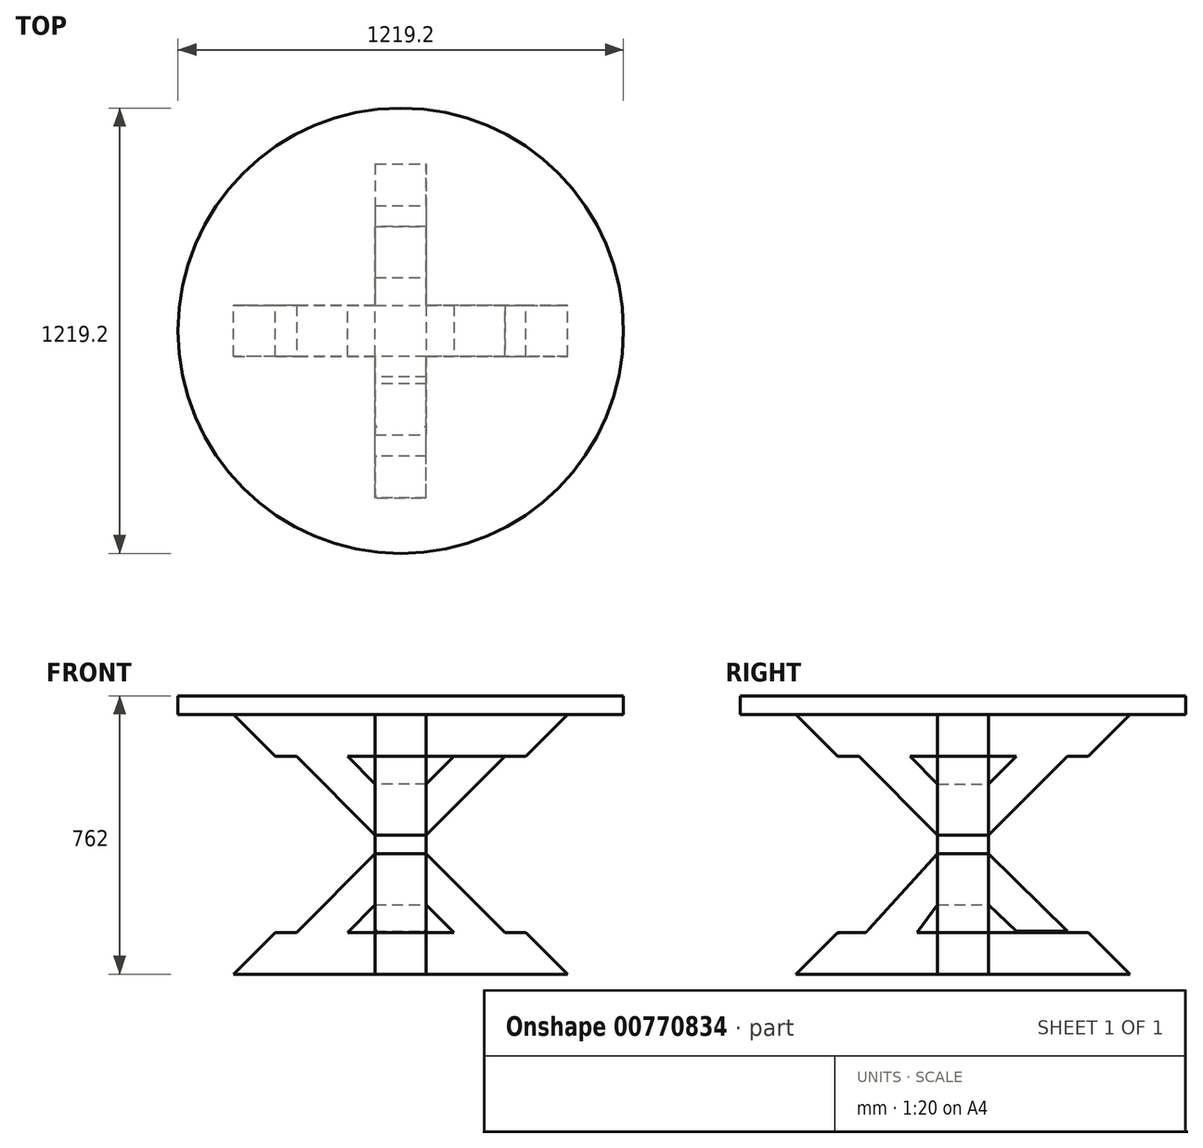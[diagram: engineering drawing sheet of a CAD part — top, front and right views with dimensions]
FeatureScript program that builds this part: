
annotation { "Feature Type Name" : "Feature", "Feature Type Description" : "" }
export const myFeature = defineFeature(function(context is Context, id is Id, definition is map)
    precondition{}
    {
        {
            var Q0;
            Q0=qCreatedBy(makeId("Top.planeOp"),FACE);
            var sketch = newSketch(context, id + "F0", { "sketchPlane" : qUnion([Q0])});
            skLineSegment(sketch, "E0.bottom", {"start": v(-457.2, -69.85) * mm, "end": v(457.2, -69.85) * mm});
            skLineSegment(sketch, "E0.top", {"start": v(-457.2, 69.85) * mm, "end": v(457.2, 69.85) * mm});
            skLineSegment(sketch, "E0.left", {"start": v(-457.2, -69.85) * mm, "end": v(-457.2, 69.85) * mm});
            skLineSegment(sketch, "E0.right", {"start": v(457.2, -69.85) * mm, "end": v(457.2, 69.85) * mm});
            skPoint(sketch, "E0.middle", {"position": v(0, 0) * mm});
            skSolve(sketch);
        }
        {
            var Q0;
            Q0 = qSketchRegion(id + "F0", true);
            extrude(context, id + "F1", {"entities" : qUnion([Q0]), "depth" : 38.1 * mm, "offsetDistance" : 25.4 * mm});
        }
        {
            var Q0;
            Q0=makeQuery(id+"F1.opExtrude","CAP_EDGE",EDGE,{"disambiguationData":[OSD([sQuery(id+"F0.wireOp",EDGE,"E0.left")])],"isStart":false});
            chamfer(context, id + "F2", {"entities" : qUnion([Q0]), "width" : 38.1 * mm, "tangentPropagation" : true});
        }
        {
            var Q0;
            Q0=makeQuery(id+"F1.opExtrude","CAP_EDGE",EDGE,{"disambiguationData":[OSD([sQuery(id+"F0.wireOp",EDGE,"E0.right")])],"isStart":false});
            chamfer(context, id + "F3", {"entities" : qUnion([Q0]), "width" : 38.1 * mm, "tangentPropagation" : true});
        }
        {
            var Q0;
            Q0=makeQuery(id+"F1.opExtrude","CAP_FACE",FACE,{"disambiguationData":[OSD([sQuery(id+"F0.wireOp",EDGE,"E0.bottom"),sQuery(id+"F0.wireOp",EDGE,"E0.top"),sQuery(id+"F0.wireOp",EDGE,"E0.left"),sQuery(id+"F0.wireOp",EDGE,"E0.right")])],"isStart":false});
            var sketch = newSketch(context, id + "F4", { "sketchPlane" : qUnion([Q0])});
            skLineSegment(sketch, "E1.bottom", {"start": v(419.1, 69.85) * mm, "end": v(-419.1, 69.85) * mm});
            skLineSegment(sketch, "E1.top", {"start": v(419.1, -69.85) * mm, "end": v(-419.1, -69.85) * mm});
            skLineSegment(sketch, "E1.left", {"start": v(419.1, 69.85) * mm, "end": v(419.1, -69.85) * mm});
            skLineSegment(sketch, "E1.right", {"start": v(-419.1, 69.85) * mm, "end": v(-419.1, -69.85) * mm});
            skPoint(sketch, "E1.middle", {"position": v(0, 0) * mm});
            skSolve(sketch);
        }
        {
            var Q0;
            Q0 = qSketchRegion(id + "F4", true);
            extrude(context, id + "F5", {"entities" : qUnion([Q0]), "operationType" : NewBodyOperationType.ADD, "depth" : 38.1 * mm, "offsetDistance" : 25.4 * mm});
        }
        {
            var Q0;
            Q0=makeQuery(id+"F5.opExtrude","CAP_EDGE",EDGE,{"disambiguationData":[OSD([sQuery(id+"F4.wireOp",EDGE,"E1.right")])],"isStart":false});
            chamfer(context, id + "F6", {"entities" : qUnion([Q0]), "width" : 38.1 * mm, "tangentPropagation" : true});
        }
        {
            var Q0;
            Q0=makeQuery(id+"F5.opExtrude","CAP_EDGE",EDGE,{"disambiguationData":[OSD([sQuery(id+"F4.wireOp",EDGE,"E1.left")])],"isStart":false});
            chamfer(context, id + "F7", {"entities" : qUnion([Q0]), "width" : 38.1 * mm, "tangentPropagation" : true});
        }
        {
            var Q0;
            Q0=makeQuery(id+"F5.opExtrude","CAP_FACE",FACE,{"disambiguationData":[OSD([sQuery(id+"F4.wireOp",EDGE,"E1.bottom"),sQuery(id+"F4.wireOp",EDGE,"E1.top"),sQuery(id+"F4.wireOp",EDGE,"E1.left"),sQuery(id+"F4.wireOp",EDGE,"E1.right")])],"isStart":false});
            var sketch = newSketch(context, id + "F8", { "sketchPlane" : qUnion([Q0])});
            skLineSegment(sketch, "E2.bottom", {"start": v(-381, 69.85) * mm, "end": v(381, 69.85) * mm});
            skLineSegment(sketch, "E2.top", {"start": v(-381, -69.85) * mm, "end": v(381, -69.85) * mm});
            skLineSegment(sketch, "E2.left", {"start": v(-381, 69.85) * mm, "end": v(-381, -69.85) * mm});
            skLineSegment(sketch, "E2.right", {"start": v(381, 69.85) * mm, "end": v(381, -69.85) * mm});
            skPoint(sketch, "E2.middle", {"position": v(0, 0) * mm});
            skSolve(sketch);
        }
        {
            var Q0;
            Q0 = qSketchRegion(id + "F8", true);
            extrude(context, id + "F9", {"entities" : qUnion([Q0]), "operationType" : NewBodyOperationType.ADD, "depth" : 38.1 * mm, "offsetDistance" : 25.4 * mm});
        }
        {
            var Q0;
            Q0=makeQuery(id+"F9.opExtrude","CAP_EDGE",EDGE,{"disambiguationData":[OSD([sQuery(id+"F8.wireOp",EDGE,"E2.left")])],"isStart":false});
            var Q1;
            Q1=makeQuery(id+"F9.opExtrude","CAP_EDGE",EDGE,{"disambiguationData":[OSD([sQuery(id+"F8.wireOp",EDGE,"E2.right")])],"isStart":false});
            chamfer(context, id + "F10", {"entities" : qUnion([Q0, Q1]), "width" : 38.1 * mm, "tangentPropagation" : true});
        }
        {
            var Q0;
            Q0=makeQuery(id+"F9.boolean.opBoolean","MERGE",FACE,{"derivedFrom":[makeQuery(id+"F5.boolean.opBoolean","MERGE",FACE,{"derivedFrom":[makeQuery(id+"F1.opExtrude","SWEPT_FACE",FACE,{"disambiguationData":[OSD([sQuery(id+"F0.wireOp",EDGE,"E0.bottom")])]}),makeQuery(id+"F5.opExtrude","SWEPT_FACE",FACE,{"disambiguationData":[OSD([sQuery(id+"F4.wireOp",EDGE,"E1.top")])]})]}),makeQuery(id+"F9.opExtrude","SWEPT_FACE",FACE,{"disambiguationData":[OSD([sQuery(id+"F8.wireOp",EDGE,"E2.top")])]})]});
            var sketch = newSketch(context, id + "F11", { "sketchPlane" : qUnion([Q0])});
            skLineSegment(sketch, "E3.bottom", {"start": v(-69.85, 0) * mm, "end": v(69.85, 0) * mm});
            skLineSegment(sketch, "E3.top", {"start": v(-69.85, 114.3) * mm, "end": v(69.85, 114.3) * mm});
            skLineSegment(sketch, "E3.left", {"start": v(-69.85, 0) * mm, "end": v(-69.85, 114.3) * mm});
            skLineSegment(sketch, "E3.right", {"start": v(69.85, 0) * mm, "end": v(69.85, 114.3) * mm});
            skSolve(sketch);
        }
        {
            var Q0;
            Q0 = qSketchRegion(id + "F11", true);
            var Q1;
            Q1=makeQuery(id+"F11.imprint","IMPRINT",FACE,{"disambiguationData":[TD([[makeQuery(id+"F11.imprint","IMPRINT",EDGE,{"derivedFrom":sQuery(id+"F11.wireOp",EDGE,"E3.bottom")}),1.0]])]});
            extrude(context, id + "F12", {"entities" : qUnion([Q0, Q1]), "operationType" : NewBodyOperationType.ADD, "depth" : 387.35 * mm, "offsetDistance" : 25.4 * mm});
        }
        {
            var Q0;
            Q0=makeQuery(id+"F12.opExtrude","CAP_EDGE",EDGE,{"disambiguationData":[OSD([sQuery(id+"F11.wireOp",EDGE,"E3.top")])],"isStart":false});
            chamfer(context, id + "F13", {"entities" : qUnion([Q0]), "width" : 114.3 * mm, "tangentPropagation" : true});
        }
        {
            var Q0;
            Q0=makeQuery(id+"F9.boolean.opBoolean","MERGE",FACE,{"derivedFrom":[makeQuery(id+"F5.boolean.opBoolean","MERGE",FACE,{"derivedFrom":[makeQuery(id+"F1.opExtrude","SWEPT_FACE",FACE,{"disambiguationData":[OSD([sQuery(id+"F0.wireOp",EDGE,"E0.top")])]}),makeQuery(id+"F5.opExtrude","SWEPT_FACE",FACE,{"disambiguationData":[OSD([sQuery(id+"F4.wireOp",EDGE,"E1.bottom")])]})]}),makeQuery(id+"F9.opExtrude","SWEPT_FACE",FACE,{"disambiguationData":[OSD([sQuery(id+"F8.wireOp",EDGE,"E2.bottom")])]})]});
            var sketch = newSketch(context, id + "F14", { "sketchPlane" : qUnion([Q0])});
            skLineSegment(sketch, "E4.bottom", {"start": v(-69.85, 0) * mm, "end": v(69.85, 0) * mm});
            skLineSegment(sketch, "E4.top", {"start": v(-69.85, 114.3) * mm, "end": v(69.85, 114.3) * mm});
            skLineSegment(sketch, "E4.left", {"start": v(-69.85, 0) * mm, "end": v(-69.85, 114.3) * mm});
            skLineSegment(sketch, "E4.right", {"start": v(69.85, 0) * mm, "end": v(69.85, 114.3) * mm});
            skSolve(sketch);
        }
        {
            var Q0;
            Q0=makeQuery(id+"F14.imprint","IMPRINT",FACE,{"disambiguationData":[TD([[makeQuery(id+"F14.imprint","IMPRINT",EDGE,{"derivedFrom":sQuery(id+"F14.wireOp",EDGE,"E4.bottom")}),-1.0]])]});
            extrude(context, id + "F15", {"entities" : qUnion([Q0]), "operationType" : NewBodyOperationType.ADD, "depth" : 387.35 * mm, "offsetDistance" : 25.4 * mm});
        }
        {
            var Q0;
            Q0=makeQuery(id+"F15.opExtrude","CAP_EDGE",EDGE,{"disambiguationData":[OSD([sQuery(id+"F14.wireOp",EDGE,"E4.top")])],"isStart":false});
            chamfer(context, id + "F16", {"entities" : qUnion([Q0]), "width" : 114.3 * mm, "tangentPropagation" : true});
        }
        {
            var Q0;
            Q0=makeQuery(id+"F15.boolean.opBoolean","MERGE",FACE,{"derivedFrom":[makeQuery(id+"F12.boolean.opBoolean","MERGE",FACE,{"derivedFrom":[makeQuery(id+"F9.opExtrude","CAP_FACE",FACE,{"disambiguationData":[OSD([sQuery(id+"F8.wireOp",EDGE,"E2.bottom"),sQuery(id+"F8.wireOp",EDGE,"E2.top"),sQuery(id+"F8.wireOp",EDGE,"E2.left"),sQuery(id+"F8.wireOp",EDGE,"E2.right")])],"isStart":false}),makeQuery(id+"F12.opExtrude","SWEPT_FACE",FACE,{"disambiguationData":[OSD([sQuery(id+"F11.wireOp",EDGE,"E3.top")])]})]}),makeQuery(id+"F15.opExtrude","SWEPT_FACE",FACE,{"disambiguationData":[OSD([sQuery(id+"F14.wireOp",EDGE,"E4.top")])]})]});
            var sketch = newSketch(context, id + "F17", { "sketchPlane" : qUnion([Q0])});
            skLineSegment(sketch, "E5.bottom", {"start": v(-69.85, -69.85) * mm, "end": v(69.85, -69.85) * mm});
            skLineSegment(sketch, "E5.top", {"start": v(-69.85, 69.85) * mm, "end": v(69.85, 69.85) * mm});
            skLineSegment(sketch, "E5.left", {"start": v(-69.85, -69.85) * mm, "end": v(-69.85, 69.85) * mm});
            skLineSegment(sketch, "E5.right", {"start": v(69.85, -69.85) * mm, "end": v(69.85, 69.85) * mm});
            skPoint(sketch, "E5.middle", {"position": v(0, 0) * mm});
            skSolve(sketch);
        }
        {
            var Q0;
            Q0=makeQuery(id+"F17.imprint","IMPRINT",FACE,{"disambiguationData":[TD([[makeQuery(id+"F17.imprint","IMPRINT",EDGE,{"derivedFrom":sQuery(id+"F17.wireOp",EDGE,"E5.bottom")}),1.0]])]});
            var Q1;
            Q1 = qSketchRegion(id + "F17", true);
            extrude(context, id + "F18", {"entities" : qUnion([Q0, Q1]), "operationType" : NewBodyOperationType.ADD, "depth" : 482.6 * mm, "offsetDistance" : 25.4 * mm});
        }
        {
            var Q0;
            Q0=makeQuery(id+"F18.opExtrude","CAP_FACE",FACE,{"disambiguationData":[OSD([sQuery(id+"F17.wireOp",EDGE,"E5.bottom"),sQuery(id+"F17.wireOp",EDGE,"E5.top"),sQuery(id+"F17.wireOp",EDGE,"E5.left"),sQuery(id+"F17.wireOp",EDGE,"E5.right")])],"isStart":false});
            var sketch = newSketch(context, id + "F19", { "sketchPlane" : qUnion([Q0])});
            skLineSegment(sketch, "E6.bottom", {"start": v(457.2, 69.85) * mm, "end": v(-457.2, 69.85) * mm});
            skLineSegment(sketch, "E6.top", {"start": v(457.2, -69.85) * mm, "end": v(-457.2, -69.85) * mm});
            skLineSegment(sketch, "E6.left", {"start": v(457.2, 69.85) * mm, "end": v(457.2, -69.85) * mm});
            skLineSegment(sketch, "E6.right", {"start": v(-457.2, 69.85) * mm, "end": v(-457.2, -69.85) * mm});
            skPoint(sketch, "E6.middle", {"position": v(0, 0) * mm});
            skPoint(sketch, "E6.cornerSnap0", {"position": v(0, 69.85) * mm});
            skSolve(sketch);
        }
        {
            var Q0;
            Q0 = qSketchRegion(id + "F19", true);
            extrude(context, id + "F20", {"entities" : qUnion([Q0]), "operationType" : NewBodyOperationType.ADD, "depth" : 114.3 * mm, "offsetDistance" : 25.4 * mm});
        }
        {
            var Q0;
            Q0=makeQuery(id+"F20.opExtrude","CAP_EDGE",EDGE,{"disambiguationData":[OSD([sQuery(id+"F19.wireOp",EDGE,"E6.left")])],"isStart":true});
            chamfer(context, id + "F21", {"entities" : qUnion([Q0]), "width" : 114.3 * mm, "tangentPropagation" : true});
        }
        {
            var Q0;
            Q0=makeQuery(id+"F20.opExtrude","CAP_EDGE",EDGE,{"disambiguationData":[OSD([sQuery(id+"F19.wireOp",EDGE,"E6.right")])],"isStart":true});
            chamfer(context, id + "F22", {"entities" : qUnion([Q0]), "width" : 114.3 * mm, "tangentPropagation" : true});
        }
        {
            var Q0;
            Q0=makeQuery(id+"F20.boolean.opBoolean","MERGE",FACE,{"derivedFrom":[makeQuery(id+"F18.opExtrude","SWEPT_FACE",FACE,{"disambiguationData":[OSD([sQuery(id+"F17.wireOp",EDGE,"E5.top")])]}),makeQuery(id+"F20.opExtrude","SWEPT_FACE",FACE,{"disambiguationData":[OSD([sQuery(id+"F19.wireOp",EDGE,"E6.bottom")])]})]});
            var sketch = newSketch(context, id + "F23", { "sketchPlane" : qUnion([Q0])});
            skLineSegment(sketch, "E7.bottom", {"start": v(-69.85, 596.9) * mm, "end": v(69.85, 596.9) * mm});
            skLineSegment(sketch, "E7.top", {"start": v(-69.85, 711.2) * mm, "end": v(69.85, 711.2) * mm});
            skLineSegment(sketch, "E7.left", {"start": v(-69.85, 596.9) * mm, "end": v(-69.85, 711.2) * mm});
            skLineSegment(sketch, "E7.right", {"start": v(69.85, 596.9) * mm, "end": v(69.85, 711.2) * mm});
            skSolve(sketch);
        }
        {
            var Q0;
            Q0 = qSketchRegion(id + "F23", true);
            extrude(context, id + "F24", {"entities" : qUnion([Q0]), "operationType" : NewBodyOperationType.ADD, "depth" : 387.35 * mm, "offsetDistance" : 25.4 * mm});
        }
        {
            var Q0;
            Q0=makeQuery(id+"F24.opExtrude","CAP_EDGE",EDGE,{"disambiguationData":[OSD([sQuery(id+"F23.wireOp",EDGE,"E7.bottom")])],"isStart":false});
            chamfer(context, id + "F25", {"entities" : qUnion([Q0]), "width" : 114.3 * mm, "tangentPropagation" : true});
        }
        {
            var Q0;
            Q0=makeQuery(id+"F20.boolean.opBoolean","MERGE",FACE,{"derivedFrom":[makeQuery(id+"F18.opExtrude","SWEPT_FACE",FACE,{"disambiguationData":[OSD([sQuery(id+"F17.wireOp",EDGE,"E5.bottom")])]}),makeQuery(id+"F20.opExtrude","SWEPT_FACE",FACE,{"disambiguationData":[OSD([sQuery(id+"F19.wireOp",EDGE,"E6.top")])]})]});
            var sketch = newSketch(context, id + "F26", { "sketchPlane" : qUnion([Q0])});
            skLineSegment(sketch, "E8.bottom", {"start": v(-69.85, 596.9) * mm, "end": v(69.85, 596.9) * mm});
            skLineSegment(sketch, "E8.top", {"start": v(-69.85, 711.2) * mm, "end": v(69.85, 711.2) * mm});
            skLineSegment(sketch, "E8.left", {"start": v(-69.85, 596.9) * mm, "end": v(-69.85, 711.2) * mm});
            skLineSegment(sketch, "E8.right", {"start": v(69.85, 596.9) * mm, "end": v(69.85, 711.2) * mm});
            skSolve(sketch);
        }
        {
            var Q0;
            Q0 = qSketchRegion(id + "F26", true);
            extrude(context, id + "F27", {"entities" : qUnion([Q0]), "operationType" : NewBodyOperationType.ADD, "depth" : 387.35 * mm, "offsetDistance" : 25.4 * mm});
        }
        {
            var Q0;
            Q0=makeQuery(id+"F27.opExtrude","CAP_EDGE",EDGE,{"disambiguationData":[OSD([sQuery(id+"F26.wireOp",EDGE,"E8.bottom")])],"isStart":false});
            chamfer(context, id + "F28", {"entities" : qUnion([Q0]), "width" : 114.3 * mm, "tangentPropagation" : true});
        }
        {
            var Q0;
            Q0=makeQuery(id+"F27.boolean.opBoolean","MERGE",FACE,{"derivedFrom":[makeQuery(id+"F24.boolean.opBoolean","MERGE",FACE,{"derivedFrom":[makeQuery(id+"F20.opExtrude","CAP_FACE",FACE,{"disambiguationData":[OSD([sQuery(id+"F19.wireOp",EDGE,"E6.bottom"),sQuery(id+"F19.wireOp",EDGE,"E6.top"),sQuery(id+"F19.wireOp",EDGE,"E6.left"),sQuery(id+"F19.wireOp",EDGE,"E6.right")])],"isStart":false}),makeQuery(id+"F24.opExtrude","SWEPT_FACE",FACE,{"disambiguationData":[OSD([sQuery(id+"F23.wireOp",EDGE,"E7.top")])]})]}),makeQuery(id+"F27.opExtrude","SWEPT_FACE",FACE,{"disambiguationData":[OSD([sQuery(id+"F26.wireOp",EDGE,"E8.top")])]})]});
            var sketch = newSketch(context, id + "F29", { "sketchPlane" : qUnion([Q0])});
            skCircle(sketch, "E9", {"center": v(0, 0) * mm, "radius": 609.6 * mm});
            skSolve(sketch);
        }
        {
            var Q0;
            Q0 = qSketchRegion(id + "F29", true);
            extrude(context, id + "F30", {"entities" : qUnion([Q0]), "operationType" : NewBodyOperationType.ADD, "depth" : 50.8 * mm, "offsetDistance" : 25.4 * mm});
        }
        {
            var Q0;
            {var subQ1=makeQuery(id+"F18.opExtrude","SWEPT_FACE",FACE,{"disambiguationData":[OSD([sQuery(id+"F17.wireOp",EDGE,"E5.bottom")])]});var subQ2=sQuery(id+"F19.wireOp",EDGE,"E6.top");var subQ3=makeQuery(id+"F20.opExtrude","SWEPT_FACE",FACE,{"disambiguationData":[OSD([subQ2])]});Q0=makeQuery(id+"F27.boolean.opBoolean","SPLIT",FACE,{"disambiguationData":[TD([makeQuery(id+"F1.opExtrude","SWEPT_FACE",FACE,{"disambiguationData":[OSD([sQuery(id+"F0.wireOp",EDGE,"E0.bottom")])]})])],"derivedFrom":makeQuery(id+"F20.boolean.opBoolean","MERGE",FACE,{"derivedFrom":[subQ1,subQ3]})});}
            var sketch = newSketch(context, id + "F31", { "sketchPlane" : qUnion([Q0])});
            skLineSegment(sketch, "E10", {"start": v(69.85, 330.2) * mm, "end": v(69.85, 190.5) * mm});
            skLineSegment(sketch, "E11", {"start": v(69.85, 190.5) * mm, "end": v(146.05, 113.3) * mm});
            skLineSegment(sketch, "E12", {"start": v(146.05, 113.3) * mm, "end": v(285.75, 113.3) * mm});
            skLineSegment(sketch, "E13", {"start": v(285.75, 113.3) * mm, "end": v(69.85, 330.2) * mm});
            skSolve(sketch);
        }
        {
            var Q0;
            Q0 = qSketchRegion(id + "F31", true);
            extrude(context, id + "F32", {"entities" : qUnion([Q0]), "operationType" : NewBodyOperationType.ADD, "oppositeDirection" : true, "depth" : 139.7 * mm, "offsetDistance" : 25.4 * mm});
        }
        {
            var Q0;
            {var subQ1=sQuery(id+"F0.wireOp",EDGE,"E0.top");var subQ2=makeQuery(id+"F1.opExtrude","SWEPT_FACE",FACE,{"disambiguationData":[OSD([subQ1])]});var subQ3=makeQuery(id+"F18.opExtrude","SWEPT_FACE",FACE,{"disambiguationData":[OSD([sQuery(id+"F17.wireOp",EDGE,"E5.top")])]});var subQ6=sQuery(id+"F8.wireOp",EDGE,"E2.bottom");var subQ8=makeQuery(id+"F5.opExtrude","SWEPT_FACE",FACE,{"disambiguationData":[OSD([sQuery(id+"F4.wireOp",EDGE,"E1.bottom")])]});var subQ9=makeQuery(id+"F9.opExtrude","SWEPT_FACE",FACE,{"disambiguationData":[OSD([subQ6])]});var subQ10=sQuery(id+"F19.wireOp",EDGE,"E6.bottom");var subQ11=makeQuery(id+"F20.opExtrude","SWEPT_FACE",FACE,{"disambiguationData":[OSD([subQ10])]});var subQ12=sQuery(id+"F0.wireOp",EDGE,"E0.right");Q0=makeQuery(id+"F32.boolean.opBoolean","MERGE",FACE,{"derivedFrom":[makeQuery(id+"F15.boolean.opBoolean","SPLIT",FACE,{"disambiguationData":[TD([makeQuery(id+"F3.opChamfer","BLEND_FACE",FACE,{"disambiguationData":[OSD([subQ12])]})])],"derivedFrom":makeQuery(id+"F9.boolean.opBoolean","MERGE",FACE,{"derivedFrom":[makeQuery(id+"F5.boolean.opBoolean","MERGE",FACE,{"derivedFrom":[subQ2,subQ8]}),subQ9]})}),makeQuery(id+"F24.boolean.opBoolean","SPLIT",FACE,{"disambiguationData":[TD([subQ2])],"derivedFrom":makeQuery(id+"F20.boolean.opBoolean","MERGE",FACE,{"derivedFrom":[subQ3,subQ11]})}),makeQuery(id+"F32.opExtrude","CAP_FACE",FACE,{"disambiguationData":[OSD([sQuery(id+"F31.wireOp",EDGE,"E10"),sQuery(id+"F31.wireOp",EDGE,"E11"),sQuery(id+"F31.wireOp",EDGE,"E12"),sQuery(id+"F31.wireOp",EDGE,"E13")])],"isStart":false})]});}
            var sketch = newSketch(context, id + "F33", { "sketchPlane" : qUnion([Q0])});
            skLineSegment(sketch, "E14", {"start": v(69.85, 330.2) * mm, "end": v(69.85, 190.5) * mm});
            skLineSegment(sketch, "E15", {"start": v(69.85, 190.5) * mm, "end": v(146.05, 113.11) * mm});
            skLineSegment(sketch, "E16", {"start": v(146.05, 113.11) * mm, "end": v(285.75, 113.11) * mm});
            skLineSegment(sketch, "E17", {"start": v(285.75, 113.11) * mm, "end": v(69.85, 330.2) * mm});
            skSolve(sketch);
        }
        {
            var Q0;
            Q0=makeQuery(id+"F33.imprint","IMPRINT",FACE,{"disambiguationData":[TD([[makeQuery(id+"F33.imprint","IMPRINT",EDGE,{"derivedFrom":sQuery(id+"F33.wireOp",EDGE,"E14")}),1.0]])]});
            extrude(context, id + "F34", {"entities" : qUnion([Q0]), "operationType" : NewBodyOperationType.ADD, "oppositeDirection" : true, "depth" : 139.7 * mm, "offsetDistance" : 25.4 * mm});
        }
        {
            var Q0;
            Q0=makeQuery(id+"F32.boolean.opBoolean","SPLIT",FACE,{"disambiguationData":[TD([makeQuery(id+"F12.opExtrude","SWEPT_FACE",FACE,{"disambiguationData":[OSD([sQuery(id+"F11.wireOp",EDGE,"E3.top")])]})])],"derivedFrom":makeQuery(id+"F18.opExtrude","SWEPT_FACE",FACE,{"disambiguationData":[OSD([sQuery(id+"F17.wireOp",EDGE,"E5.right")])]})});
            var sketch = newSketch(context, id + "F35", { "sketchPlane" : qUnion([Q0])});
            skLineSegment(sketch, "E18", {"start": v(-69.85, 190.5) * mm, "end": v(-69.85, 330.2) * mm});
            skLineSegment(sketch, "E19", {"start": v(-69.85, 330.2) * mm, "end": v(-266.29, 113.51) * mm});
            skLineSegment(sketch, "E20", {"start": v(-266.29, 113.51) * mm, "end": v(-126.59, 113.51) * mm});
            skLineSegment(sketch, "E21", {"start": v(-126.59, 113.51) * mm, "end": v(-69.85, 190.5) * mm});
            skSolve(sketch);
        }
        {
            var Q0;
            Q0=makeQuery(id+"F35.imprint","IMPRINT",FACE,{"disambiguationData":[TD([[makeQuery(id+"F35.imprint","IMPRINT",EDGE,{"derivedFrom":sQuery(id+"F35.wireOp",EDGE,"E18")}),1.0]])]});
            extrude(context, id + "F36", {"entities" : qUnion([Q0]), "operationType" : NewBodyOperationType.ADD, "oppositeDirection" : true, "depth" : 139.7 * mm, "offsetDistance" : 25.4 * mm});
        }
        {
            var Q0;
            Q0=makeQuery(id+"F32.boolean.opBoolean","SPLIT",FACE,{"disambiguationData":[TD([makeQuery(id+"F12.opExtrude","SWEPT_FACE",FACE,{"disambiguationData":[OSD([sQuery(id+"F11.wireOp",EDGE,"E3.top")])]})])],"derivedFrom":makeQuery(id+"F18.opExtrude","SWEPT_FACE",FACE,{"disambiguationData":[OSD([sQuery(id+"F17.wireOp",EDGE,"E5.right")])]})});
            var sketch = newSketch(context, id + "F37", { "sketchPlane" : qUnion([Q0])});
            skLineSegment(sketch, "E22", {"start": v(69.85, 190.5) * mm, "end": v(69.85, 330.2) * mm});
            skLineSegment(sketch, "E23", {"start": v(69.85, 330.2) * mm, "end": v(285.75, 117.73) * mm});
            skLineSegment(sketch, "E24", {"start": v(285.75, 117.73) * mm, "end": v(146.05, 117.73) * mm});
            skLineSegment(sketch, "E25", {"start": v(146.05, 117.73) * mm, "end": v(69.85, 190.5) * mm});
            skSolve(sketch);
        }
        {
            var Q0;
            Q0=makeQuery(id+"F37.imprint","IMPRINT",FACE,{"disambiguationData":[TD([[makeQuery(id+"F37.imprint","IMPRINT",EDGE,{"derivedFrom":sQuery(id+"F37.wireOp",EDGE,"E22")}),-1.0]])]});
            extrude(context, id + "F38", {"entities" : qUnion([Q0]), "operationType" : NewBodyOperationType.ADD, "oppositeDirection" : true, "depth" : 139.7 * mm, "offsetDistance" : 25.4 * mm});
        }
        {
            var Q0;
            Q0=makeQuery(id+"F34.boolean.opBoolean","SPLIT",FACE,{"disambiguationData":[TD([makeQuery(id+"F24.opExtrude","SWEPT_FACE",FACE,{"disambiguationData":[OSD([sQuery(id+"F23.wireOp",EDGE,"E7.bottom")])]})])],"derivedFrom":makeQuery(id+"F18.opExtrude","SWEPT_FACE",FACE,{"disambiguationData":[OSD([sQuery(id+"F17.wireOp",EDGE,"E5.left")])]})});
            var sketch = newSketch(context, id + "F39", { "sketchPlane" : qUnion([Q0])});
            skLineSegment(sketch, "E26", {"start": v(69.85, 381) * mm, "end": v(285.75, 597) * mm});
            skLineSegment(sketch, "E27", {"start": v(285.75, 597) * mm, "end": v(146.05, 597) * mm});
            skLineSegment(sketch, "E28", {"start": v(146.05, 597) * mm, "end": v(69.85, 520.7) * mm});
            skLineSegment(sketch, "E29", {"start": v(69.85, 520.7) * mm, "end": v(69.85, 381) * mm});
            skSolve(sketch);
        }
        {
            var Q0;
            {var subQ0=makeQuery(id+"F24.opExtrude","SWEPT_FACE",FACE,{"disambiguationData":[OSD([sQuery(id+"F23.wireOp",EDGE,"E7.left")])]});var subQ1=sQuery(id+"F19.wireOp",EDGE,"E6.bottom");var subQ2=makeQuery(id+"F20.opExtrude","CAP_FACE",FACE,{"disambiguationData":[OSD([subQ1,sQuery(id+"F19.wireOp",EDGE,"E6.top"),sQuery(id+"F19.wireOp",EDGE,"E6.left"),sQuery(id+"F19.wireOp",EDGE,"E6.right")])],"isStart":true});var subQ3=sQuery(id+"F31.wireOp",EDGE,"E13");var subQ4=makeQuery(id+"F20.opExtrude","SWEPT_FACE",FACE,{"disambiguationData":[OSD([subQ1])]});var subQ5=makeQuery(id+"F18.opExtrude","SWEPT_FACE",FACE,{"disambiguationData":[OSD([sQuery(id+"F17.wireOp",EDGE,"E5.right")])]});var subQ6=sQuery(id+"F37.wireOp",EDGE,"E23");var subQ7=makeQuery(id+"F18.opExtrude","SWEPT_FACE",FACE,{"disambiguationData":[OSD([sQuery(id+"F17.wireOp",EDGE,"E5.left")])]});var subQ8=sQuery(id+"F0.wireOp",EDGE,"E0.top");var subQ9=makeQuery(id+"F1.opExtrude","SWEPT_FACE",FACE,{"disambiguationData":[OSD([subQ8])]});var subQ10=sQuery(id+"F33.wireOp",EDGE,"E17");var subQ11=sQuery(id+"F37.wireOp",EDGE,"E25");var subQ12=sQuery(id+"F37.wireOp",EDGE,"E24");var subQ13=sQuery(id+"F37.wireOp",EDGE,"E22");var subQ14=makeQuery(id+"F24.opExtrude","SWEPT_FACE",FACE,{"disambiguationData":[OSD([sQuery(id+"F23.wireOp",EDGE,"E7.bottom")])]});var subQ15=makeQuery(id+"F5.opExtrude","SWEPT_FACE",FACE,{"disambiguationData":[OSD([sQuery(id+"F4.wireOp",EDGE,"E1.bottom")])]});var subQ16=makeQuery(id+"F34.opExtrude","CAP_FACE",FACE,{"disambiguationData":[OSD([sQuery(id+"F33.wireOp",EDGE,"E14"),sQuery(id+"F33.wireOp",EDGE,"E15"),sQuery(id+"F33.wireOp",EDGE,"E16"),subQ10])],"isStart":true});var subQ17=sQuery(id+"F8.wireOp",EDGE,"E2.bottom");var subQ18=makeQuery(id+"F9.opExtrude","SWEPT_FACE",FACE,{"disambiguationData":[OSD([subQ17])]});var subQ19=makeQuery(id+"F18.opExtrude","SWEPT_FACE",FACE,{"disambiguationData":[OSD([sQuery(id+"F17.wireOp",EDGE,"E5.top")])]});var subQ20=makeQuery(id+"F24.opExtrude","SWEPT_FACE",FACE,{"disambiguationData":[OSD([sQuery(id+"F23.wireOp",EDGE,"E7.right")])]});var subQ21=makeQuery(id+"F32.opExtrude","CAP_FACE",FACE,{"disambiguationData":[OSD([sQuery(id+"F31.wireOp",EDGE,"E10"),sQuery(id+"F31.wireOp",EDGE,"E11"),sQuery(id+"F31.wireOp",EDGE,"E12"),subQ3])],"isStart":false});var subQ27=sQuery(id+"F0.wireOp",EDGE,"E0.right");var subQ29=sQuery(id+"F0.wireOp",EDGE,"E0.left");var subQ32=makeQuery(id+"F9.boolean.opBoolean","MERGE",FACE,{"derivedFrom":[makeQuery(id+"F5.boolean.opBoolean","MERGE",FACE,{"derivedFrom":[subQ9,subQ15]}),subQ18]});Q0=makeQuery(id+"F38.boolean.opBoolean","SPLIT",FACE,{"disambiguationData":[TD([subQ9,subQ15,subQ18,subQ19,subQ7,subQ5,subQ4,subQ2,subQ14,subQ0,subQ20,subQ21,makeQuery(id+"F32.opExtrude","SWEPT_FACE",FACE,{"disambiguationData":[OSD([subQ3])]}),subQ16,makeQuery(id+"F34.opExtrude","SWEPT_FACE",FACE,{"disambiguationData":[OSD([subQ10])]}),makeQuery(id+"F38.opExtrude","CAP_FACE",FACE,{"disambiguationData":[OSD([subQ13,subQ6,subQ12,subQ11])],"isStart":true}),makeQuery(id+"F38.opExtrude","CAP_FACE",FACE,{"disambiguationData":[OSD([subQ13,subQ6,subQ12,subQ11])],"isStart":false}),makeQuery(id+"F38.opExtrude","SWEPT_FACE",FACE,{"disambiguationData":[OSD([subQ6])]})])],"derivedFrom":makeQuery(id+"F34.boolean.opBoolean","MERGE",FACE,{"derivedFrom":[makeQuery(id+"F15.boolean.opBoolean","SPLIT",FACE,{"disambiguationData":[TD([makeQuery(id+"F2.opChamfer","BLEND_FACE",FACE,{"disambiguationData":[OSD([subQ29])]})])],"derivedFrom":subQ32}),makeQuery(id+"F32.boolean.opBoolean","MERGE",FACE,{"derivedFrom":[makeQuery(id+"F15.boolean.opBoolean","SPLIT",FACE,{"disambiguationData":[TD([makeQuery(id+"F3.opChamfer","BLEND_FACE",FACE,{"disambiguationData":[OSD([subQ27])]})])],"derivedFrom":subQ32}),makeQuery(id+"F24.boolean.opBoolean","SPLIT",FACE,{"disambiguationData":[TD([subQ9])],"derivedFrom":makeQuery(id+"F20.boolean.opBoolean","MERGE",FACE,{"derivedFrom":[subQ19,subQ4]})}),subQ21]}),subQ16]})});}
            var sketch = newSketch(context, id + "F40", { "sketchPlane" : qUnion([Q0])});
            skLineSegment(sketch, "E30", {"start": v(69.85, 381) * mm, "end": v(285.75, 598.13) * mm});
            skLineSegment(sketch, "E31", {"start": v(285.75, 598.13) * mm, "end": v(146.05, 598.13) * mm});
            skLineSegment(sketch, "E32", {"start": v(146.05, 598.13) * mm, "end": v(69.85, 520.7) * mm});
            skLineSegment(sketch, "E33", {"start": v(69.85, 520.7) * mm, "end": v(69.85, 381) * mm});
            skSolve(sketch);
        }
        {
            var Q0;
            Q0=makeQuery(id+"F32.boolean.opBoolean","SPLIT",FACE,{"disambiguationData":[TD([makeQuery(id+"F24.opExtrude","SWEPT_FACE",FACE,{"disambiguationData":[OSD([sQuery(id+"F23.wireOp",EDGE,"E7.bottom")])]})])],"derivedFrom":makeQuery(id+"F18.opExtrude","SWEPT_FACE",FACE,{"disambiguationData":[OSD([sQuery(id+"F17.wireOp",EDGE,"E5.right")])]})});
            var sketch = newSketch(context, id + "F41", { "sketchPlane" : qUnion([Q0])});
            skLineSegment(sketch, "E34", {"start": v(69.85, 381) * mm, "end": v(285.75, 597.78) * mm});
            skLineSegment(sketch, "E35", {"start": v(285.75, 597.78) * mm, "end": v(146.05, 597.78) * mm});
            skLineSegment(sketch, "E36", {"start": v(146.05, 597.78) * mm, "end": v(69.85, 520.7) * mm});
            skLineSegment(sketch, "E37", {"start": v(69.85, 520.7) * mm, "end": v(69.85, 381) * mm});
            skSolve(sketch);
        }
        {
            var Q0;
            Q0 = qSketchRegion(id + "F41", true);
            var Q1;
            Q1=makeQuery(id+"F41.imprint","IMPRINT",FACE,{"disambiguationData":[TD([[makeQuery(id+"F41.imprint","IMPRINT",EDGE,{"derivedFrom":sQuery(id+"F41.wireOp",EDGE,"E34")}),1.0]])]});
            extrude(context, id + "F42", {"entities" : qUnion([Q0, Q1]), "operationType" : NewBodyOperationType.ADD, "oppositeDirection" : true, "depth" : 139.7 * mm, "offsetDistance" : 25.4 * mm});
        }
        {
            var Q0;
            Q0=makeQuery(id+"F40.imprint","IMPRINT",FACE,{"disambiguationData":[TD([[makeQuery(id+"F40.imprint","IMPRINT",EDGE,{"derivedFrom":sQuery(id+"F40.wireOp",EDGE,"E30")}),1.0]])]});
            extrude(context, id + "F43", {"entities" : qUnion([Q0]), "operationType" : NewBodyOperationType.ADD, "oppositeDirection" : true, "depth" : 139.7 * mm, "offsetDistance" : 25.4 * mm});
        }
        {
            var Q0;
            Q0=makeQuery(id+"F39.imprint","IMPRINT",FACE,{"disambiguationData":[TD([[makeQuery(id+"F39.imprint","IMPRINT",EDGE,{"derivedFrom":sQuery(id+"F39.wireOp",EDGE,"E26")}),1.0]])]});
            extrude(context, id + "F44", {"entities" : qUnion([Q0]), "operationType" : NewBodyOperationType.ADD, "oppositeDirection" : true, "depth" : 139.7 * mm, "offsetDistance" : 25.4 * mm});
        }
        {
            var Q0;
            {var subQ0=sQuery(id+"F19.wireOp",EDGE,"E6.top");var subQ1=makeQuery(id+"F20.opExtrude","SWEPT_FACE",FACE,{"disambiguationData":[OSD([subQ0])]});var subQ2=sQuery(id+"F19.wireOp",EDGE,"E6.right");var subQ3=sQuery(id+"F19.wireOp",EDGE,"E6.left");var subQ4=sQuery(id+"F19.wireOp",EDGE,"E6.bottom");var subQ5=makeQuery(id+"F20.opExtrude","CAP_FACE",FACE,{"disambiguationData":[OSD([subQ4,subQ0,subQ3,subQ2])],"isStart":true});var subQ6=makeQuery(id+"F18.opExtrude","SWEPT_FACE",FACE,{"disambiguationData":[OSD([sQuery(id+"F17.wireOp",EDGE,"E5.right")])]});var subQ7=makeQuery(id+"F18.opExtrude","SWEPT_FACE",FACE,{"disambiguationData":[OSD([sQuery(id+"F17.wireOp",EDGE,"E5.left")])]});var subQ8=sQuery(id+"F40.wireOp",EDGE,"E32");var subQ9=sQuery(id+"F0.wireOp",EDGE,"E0.bottom");var subQ10=makeQuery(id+"F1.opExtrude","SWEPT_FACE",FACE,{"disambiguationData":[OSD([subQ9])]});var subQ11=makeQuery(id+"F27.opExtrude","SWEPT_FACE",FACE,{"disambiguationData":[OSD([sQuery(id+"F26.wireOp",EDGE,"E8.left")])]});var subQ12=sQuery(id+"F33.wireOp",EDGE,"E17");var subQ13=makeQuery(id+"F34.opExtrude","CAP_FACE",FACE,{"disambiguationData":[OSD([sQuery(id+"F33.wireOp",EDGE,"E14"),sQuery(id+"F33.wireOp",EDGE,"E15"),sQuery(id+"F33.wireOp",EDGE,"E16"),subQ12])],"isStart":false});var subQ14=makeQuery(id+"F5.opExtrude","SWEPT_FACE",FACE,{"disambiguationData":[OSD([sQuery(id+"F4.wireOp",EDGE,"E1.top")])]});var subQ15=makeQuery(id+"F27.opExtrude","SWEPT_FACE",FACE,{"disambiguationData":[OSD([sQuery(id+"F26.wireOp",EDGE,"E8.right")])]});var subQ16=makeQuery(id+"F43.opExtrude","CAP_FACE",FACE,{"disambiguationData":[OSD([sQuery(id+"F40.wireOp",EDGE,"E30"),sQuery(id+"F40.wireOp",EDGE,"E31"),subQ8,sQuery(id+"F40.wireOp",EDGE,"E33")])],"isStart":false});var subQ17=makeQuery(id+"F18.opExtrude","SWEPT_FACE",FACE,{"disambiguationData":[OSD([sQuery(id+"F17.wireOp",EDGE,"E5.bottom")])]});var subQ18=sQuery(id+"F8.wireOp",EDGE,"E2.top");var subQ19=makeQuery(id+"F9.opExtrude","SWEPT_FACE",FACE,{"disambiguationData":[OSD([subQ18])]});var subQ20=makeQuery(id+"F27.opExtrude","SWEPT_FACE",FACE,{"disambiguationData":[OSD([sQuery(id+"F26.wireOp",EDGE,"E8.bottom")])]});var subQ21=sQuery(id+"F39.wireOp",EDGE,"E29");var subQ22=sQuery(id+"F39.wireOp",EDGE,"E28");var subQ23=sQuery(id+"F39.wireOp",EDGE,"E27");var subQ24=sQuery(id+"F39.wireOp",EDGE,"E26");var subQ25=sQuery(id+"F31.wireOp",EDGE,"E13");var subQ26=makeQuery(id+"F32.opExtrude","CAP_FACE",FACE,{"disambiguationData":[OSD([sQuery(id+"F31.wireOp",EDGE,"E10"),sQuery(id+"F31.wireOp",EDGE,"E11"),sQuery(id+"F31.wireOp",EDGE,"E12"),subQ25])],"isStart":true});var subQ27=sQuery(id+"F41.wireOp",EDGE,"E37");var subQ28=sQuery(id+"F41.wireOp",EDGE,"E36");var subQ29=sQuery(id+"F41.wireOp",EDGE,"E35");var subQ30=sQuery(id+"F41.wireOp",EDGE,"E34");var subQ31=sQuery(id+"F35.wireOp",EDGE,"E21");var subQ32=sQuery(id+"F35.wireOp",EDGE,"E20");var subQ33=sQuery(id+"F35.wireOp",EDGE,"E19");var subQ34=sQuery(id+"F35.wireOp",EDGE,"E18");var subQ35=makeQuery(id+"F12.opExtrude","SWEPT_FACE",FACE,{"disambiguationData":[OSD([sQuery(id+"F11.wireOp",EDGE,"E3.left")])]});var subQ36=makeQuery(id+"F12.opExtrude","SWEPT_FACE",FACE,{"disambiguationData":[OSD([sQuery(id+"F11.wireOp",EDGE,"E3.right")])]});var subQ39=makeQuery(id+"F20.boolean.opBoolean","MERGE",FACE,{"derivedFrom":[subQ17,subQ1]});var subQ40=sQuery(id+"F0.wireOp",EDGE,"E0.right");var subQ42=sQuery(id+"F0.wireOp",EDGE,"E0.left");var subQ44=makeQuery(id+"F9.boolean.opBoolean","MERGE",FACE,{"derivedFrom":[makeQuery(id+"F5.boolean.opBoolean","MERGE",FACE,{"derivedFrom":[subQ10,subQ14]}),subQ19]});Q0=makeQuery(id+"F44.boolean.opBoolean","SPLIT",FACE,{"disambiguationData":[TD([subQ10,subQ14,subQ19,subQ17,subQ7,subQ6,subQ5,subQ1,makeQuery(id+"F24.opExtrude","SWEPT_FACE",FACE,{"disambiguationData":[OSD([sQuery(id+"F23.wireOp",EDGE,"E7.left")])]}),makeQuery(id+"F24.opExtrude","SWEPT_FACE",FACE,{"disambiguationData":[OSD([sQuery(id+"F23.wireOp",EDGE,"E7.right")])]}),subQ20,subQ11,subQ15,subQ26,subQ13,makeQuery(id+"F42.opExtrude","CAP_FACE",FACE,{"disambiguationData":[OSD([subQ30,subQ29,subQ28,subQ27])],"isStart":true}),makeQuery(id+"F42.opExtrude","CAP_FACE",FACE,{"disambiguationData":[OSD([subQ30,subQ29,subQ28,subQ27])],"isStart":false}),subQ16,makeQuery(id+"F43.opExtrude","SWEPT_FACE",FACE,{"disambiguationData":[OSD([subQ8])]}),makeQuery(id+"F44.opExtrude","CAP_FACE",FACE,{"disambiguationData":[OSD([subQ24,subQ23,subQ22,subQ21])],"isStart":true}),makeQuery(id+"F44.opExtrude","CAP_FACE",FACE,{"disambiguationData":[OSD([subQ24,subQ23,subQ22,subQ21])],"isStart":false}),makeQuery(id+"F44.opExtrude","SWEPT_FACE",FACE,{"disambiguationData":[OSD([subQ22])]})])],"derivedFrom":makeQuery(id+"F43.boolean.opBoolean","MERGE",FACE,{"derivedFrom":[makeQuery(id+"F27.boolean.opBoolean","SPLIT",FACE,{"disambiguationData":[TD([makeQuery(id+"F22.opChamfer","BLEND_FACE",FACE,{"disambiguationData":[OSD([subQ2])]})])],"derivedFrom":subQ39}),makeQuery(id+"F36.boolean.opBoolean","SPLIT",FACE,{"disambiguationData":[TD([subQ10,subQ14,subQ19,subQ35,subQ36,subQ17,subQ7,subQ6,subQ5,subQ1,subQ20,subQ11,subQ15,subQ26,makeQuery(id+"F32.opExtrude","SWEPT_FACE",FACE,{"disambiguationData":[OSD([subQ25])]}),subQ13,makeQuery(id+"F34.opExtrude","SWEPT_FACE",FACE,{"disambiguationData":[OSD([subQ12])]}),makeQuery(id+"F36.opExtrude","CAP_FACE",FACE,{"disambiguationData":[OSD([subQ34,subQ33,subQ32,subQ31])],"isStart":true}),makeQuery(id+"F36.opExtrude","CAP_FACE",FACE,{"disambiguationData":[OSD([subQ34,subQ33,subQ32,subQ31])],"isStart":false}),makeQuery(id+"F36.opExtrude","SWEPT_FACE",FACE,{"disambiguationData":[OSD([subQ33])]})])],"derivedFrom":makeQuery(id+"F34.boolean.opBoolean","MERGE",FACE,{"derivedFrom":[makeQuery(id+"F12.boolean.opBoolean","SPLIT",FACE,{"disambiguationData":[TD([makeQuery(id+"F2.opChamfer","BLEND_FACE",FACE,{"disambiguationData":[OSD([subQ42])]})])],"derivedFrom":subQ44}),makeQuery(id+"F32.boolean.opBoolean","MERGE",FACE,{"derivedFrom":[makeQuery(id+"F12.boolean.opBoolean","SPLIT",FACE,{"disambiguationData":[TD([makeQuery(id+"F3.opChamfer","BLEND_FACE",FACE,{"disambiguationData":[OSD([subQ40])]})])],"derivedFrom":subQ44}),makeQuery(id+"F27.boolean.opBoolean","SPLIT",FACE,{"disambiguationData":[TD([subQ10])],"derivedFrom":subQ39}),subQ26]}),subQ13]})}),subQ16]})});}
            var sketch = newSketch(context, id + "F45", { "sketchPlane" : qUnion([Q0])});
            skLineSegment(sketch, "E38", {"start": v(69.85, 520.7) * mm, "end": v(69.85, 381.1) * mm});
            skLineSegment(sketch, "E39", {"start": v(69.85, 381.1) * mm, "end": v(285.75, 596.66) * mm});
            skLineSegment(sketch, "E40", {"start": v(285.75, 596.66) * mm, "end": v(146.05, 596.66) * mm});
            skLineSegment(sketch, "E41", {"start": v(146.05, 596.66) * mm, "end": v(69.85, 520.7) * mm});
            skSolve(sketch);
        }
        {
            var Q0;
            Q0=makeQuery(id+"F45.imprint","IMPRINT",FACE,{"disambiguationData":[TD([[makeQuery(id+"F45.imprint","IMPRINT",EDGE,{"derivedFrom":sQuery(id+"F45.wireOp",EDGE,"E38")}),1.0]])]});
            extrude(context, id + "F46", {"entities" : qUnion([Q0]), "operationType" : NewBodyOperationType.ADD, "oppositeDirection" : true, "depth" : 139.7 * mm, "offsetDistance" : 25.4 * mm});
        }
        {
            var Q0;
            Q0=makeQuery(id+"F13.opChamfer","BLEND_EDGE",EDGE,{"blendedFrom":[makeQuery(id+"F12.opExtrude","CAP_EDGE",EDGE,{"disambiguationData":[OSD([sQuery(id+"F11.wireOp",EDGE,"E3.top")])],"isStart":false}),makeQuery(id+"F12.opExtrude","SWEPT_FACE",FACE,{"disambiguationData":[OSD([sQuery(id+"F11.wireOp",EDGE,"E3.left")])]})],"blendedInto":[makeQuery(id+"F12.opExtrude","SWEPT_FACE",FACE,{"disambiguationData":[OSD([sQuery(id+"F11.wireOp",EDGE,"E3.left")])]})]});
            fillet(context, id + "F47", {"entities" : qUnion([Q0]), "radius" : 5.08 * mm, "tangentPropagation" : true, "allowEdgeOverflow" : false});
        }
        {
            var Q0;
            {var subQ0=sQuery(id+"F11.wireOp",EDGE,"E3.left");var subQ1=sQuery(id+"F8.wireOp",EDGE,"E2.top");var subQ2=sQuery(id+"F11.wireOp",EDGE,"E3.top");Q0=makeQuery(id+"F36.boolean.opBoolean","SPLIT",EDGE,{"disambiguationData":[TD([makeQuery(id+"F13.opChamfer","BLEND_FACE",FACE,{"disambiguationData":[OSD([subQ2])]})])],"derivedFrom":makeQuery(id+"F12.opExtrude","SWEPT_EDGE",EDGE,{"disambiguationData":[OSD([subQ1,subQ2,subQ0])]})});}
            var Q1;
            {var subQ0=sQuery(id+"F11.wireOp",EDGE,"E3.right");var subQ1=sQuery(id+"F11.wireOp",EDGE,"E3.top");var subQ3=sQuery(id+"F8.wireOp",EDGE,"E2.top");Q1=makeQuery(id+"F36.boolean.opBoolean","SPLIT",EDGE,{"disambiguationData":[TD([makeQuery(id+"F13.opChamfer","BLEND_FACE",FACE,{"disambiguationData":[OSD([subQ1])]})])],"derivedFrom":makeQuery(id+"F12.opExtrude","SWEPT_EDGE",EDGE,{"disambiguationData":[OSD([subQ3,subQ1,subQ0])]})});}
            var Q2;
            Q2=makeQuery(id+"F13.opChamfer","BLEND_EDGE",EDGE,{"blendedFrom":[makeQuery(id+"F12.opExtrude","CAP_EDGE",EDGE,{"disambiguationData":[OSD([sQuery(id+"F11.wireOp",EDGE,"E3.top")])],"isStart":false}),makeQuery(id+"F12.opExtrude","SWEPT_FACE",FACE,{"disambiguationData":[OSD([sQuery(id+"F11.wireOp",EDGE,"E3.right")])]})],"blendedInto":[makeQuery(id+"F12.opExtrude","SWEPT_FACE",FACE,{"disambiguationData":[OSD([sQuery(id+"F11.wireOp",EDGE,"E3.right")])]})]});
            var Q3;
            {var subQ0=sQuery(id+"F11.wireOp",EDGE,"E3.top");Q3=makeQuery(id+"F13.opChamfer","BLEND_EDGE",EDGE,{"blendedFrom":[makeQuery(id+"F12.opExtrude","CAP_EDGE",EDGE,{"disambiguationData":[OSD([subQ0])],"isStart":false}),makeQuery(id+"F12.boolean.opBoolean","MERGE",FACE,{"derivedFrom":[makeQuery(id+"F9.opExtrude","CAP_FACE",FACE,{"disambiguationData":[OSD([sQuery(id+"F8.wireOp",EDGE,"E2.bottom"),sQuery(id+"F8.wireOp",EDGE,"E2.top"),sQuery(id+"F8.wireOp",EDGE,"E2.left"),sQuery(id+"F8.wireOp",EDGE,"E2.right")])],"isStart":false}),makeQuery(id+"F12.opExtrude","SWEPT_FACE",FACE,{"disambiguationData":[OSD([subQ0])]})]})],"blendedInto":[makeQuery(id+"F12.boolean.opBoolean","MERGE",FACE,{"derivedFrom":[makeQuery(id+"F9.opExtrude","CAP_FACE",FACE,{"disambiguationData":[OSD([sQuery(id+"F8.wireOp",EDGE,"E2.bottom"),sQuery(id+"F8.wireOp",EDGE,"E2.top"),sQuery(id+"F8.wireOp",EDGE,"E2.left"),sQuery(id+"F8.wireOp",EDGE,"E2.right")])],"isStart":false}),makeQuery(id+"F12.opExtrude","SWEPT_FACE",FACE,{"disambiguationData":[OSD([subQ0])]})]})]});}
            var Q4;
            {var subQ0=makeQuery(id+"F15.opExtrude","SWEPT_FACE",FACE,{"disambiguationData":[OSD([sQuery(id+"F14.wireOp",EDGE,"E4.top")])]});var subQ1=sQuery(id+"F11.wireOp",EDGE,"E3.top");var subQ2=makeQuery(id+"F12.opExtrude","SWEPT_FACE",FACE,{"disambiguationData":[OSD([subQ1])]});var subQ3=sQuery(id+"F8.wireOp",EDGE,"E2.top");var subQ4=makeQuery(id+"F9.opExtrude","CAP_FACE",FACE,{"disambiguationData":[OSD([sQuery(id+"F8.wireOp",EDGE,"E2.bottom"),subQ3,sQuery(id+"F8.wireOp",EDGE,"E2.left"),sQuery(id+"F8.wireOp",EDGE,"E2.right")])],"isStart":false});Q4=makeQuery(id+"F36.boolean.opBoolean","INTERSECT",EDGE,{"derivedFrom":[makeQuery(id+"F18.boolean.opBoolean","SPLIT",FACE,{"disambiguationData":[TD([makeQuery(id+"F13.opChamfer","BLEND_FACE",FACE,{"disambiguationData":[OSD([subQ1])]})])],"derivedFrom":makeQuery(id+"F15.boolean.opBoolean","MERGE",FACE,{"derivedFrom":[makeQuery(id+"F12.boolean.opBoolean","MERGE",FACE,{"derivedFrom":[subQ4,subQ2]}),subQ0]})}),makeQuery(id+"F36.opExtrude","SWEPT_FACE",FACE,{"disambiguationData":[OSD([sQuery(id+"F35.wireOp",EDGE,"E19")])]})]});}
            fillet(context, id + "F48", {"entities" : qUnion([Q0, Q1, Q2, Q3, Q4]), "radius" : 5.08 * mm, "tangentPropagation" : true, "allowEdgeOverflow" : false});
        }
    });
